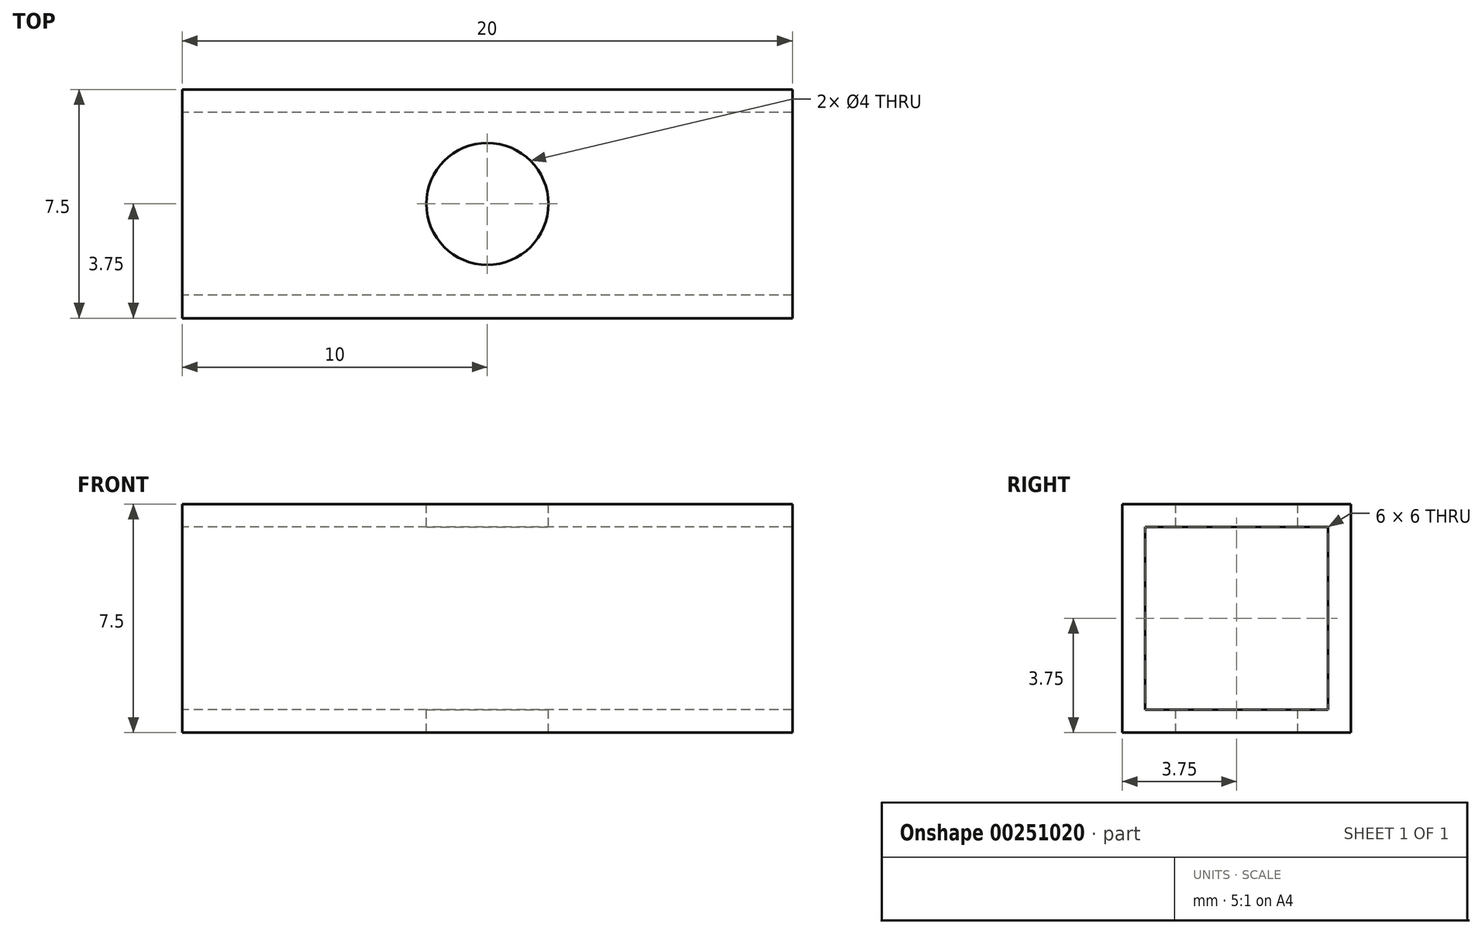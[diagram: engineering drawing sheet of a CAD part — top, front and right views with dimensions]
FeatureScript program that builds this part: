
annotation { "Feature Type Name" : "Feature", "Feature Type Description" : "" }
export const myFeature = defineFeature(function(context is Context, id is Id, definition is map)
    precondition{}
    {
        {
            var Q0;
            Q0=qCreatedBy(makeId("Right.planeOp"),FACE);
            var sketch = newSketch(context, id + "F0", { "sketchPlane" : qUnion([Q0])});
            skLineSegment(sketch, "E0.bottom", {"start": v(3.75, 3.75) * mm, "end": v(-3.75, 3.75) * mm});
            skLineSegment(sketch, "E0.top", {"start": v(3.75, -3.75) * mm, "end": v(-3.75, -3.75) * mm});
            skLineSegment(sketch, "E0.left", {"start": v(3.75, 3.75) * mm, "end": v(3.75, -3.75) * mm});
            skLineSegment(sketch, "E0.right", {"start": v(-3.75, 3.75) * mm, "end": v(-3.75, -3.75) * mm});
            skPoint(sketch, "E0.middle", {"position": v(0, 0) * mm});
            skLineSegment(sketch, "E1.bottom", {"start": v(3, 3) * mm, "end": v(-3, 3) * mm});
            skLineSegment(sketch, "E1.top", {"start": v(3, -3) * mm, "end": v(-3, -3) * mm});
            skLineSegment(sketch, "E1.left", {"start": v(3, 3) * mm, "end": v(3, -3) * mm});
            skLineSegment(sketch, "E1.right", {"start": v(-3, 3) * mm, "end": v(-3, -3) * mm});
            skSolve(sketch);
        }
        {
            var Q0;
            Q0=makeQuery(id+"F0.imprint","IMPRINT",FACE,{"disambiguationData":[TD([[makeQuery(id+"F0.imprint","IMPRINT",EDGE,{"derivedFrom":sQuery(id+"F0.wireOp",EDGE,"E0.bottom")}),1.0]])]});
            extrude(context, id + "F1", {"entities" : qUnion([Q0]), "endBound" : BoundingType.SYMMETRIC, "depth" : 20 * mm});
        }
        {
            var Q0;
            Q0=makeQuery(id+"F1.opExtrude","SWEPT_FACE",FACE,{"disambiguationData":[OSD([sQuery(id+"F0.wireOp",EDGE,"E0.bottom")])]});
            var sketch = newSketch(context, id + "F2", { "sketchPlane" : qUnion([Q0])});
            skCircle(sketch, "E2", {"center": v(0, 0) * mm, "radius": 2 * mm});
            skSolve(sketch);
        }
        {
            var Q0;
            Q0=makeQuery(id+"F2.imprint","IMPRINT",FACE,{"disambiguationData":[TD([[makeQuery(id+"F2.imprint","IMPRINT",EDGE,{"derivedFrom":sQuery(id+"F2.wireOp",EDGE,"E2")}),1.0]])]});
            extrude(context, id + "F3", {"entities" : qUnion([Q0]), "operationType" : NewBodyOperationType.REMOVE, "oppositeDirection" : true, "depth" : 25 * mm});
        }
    });
